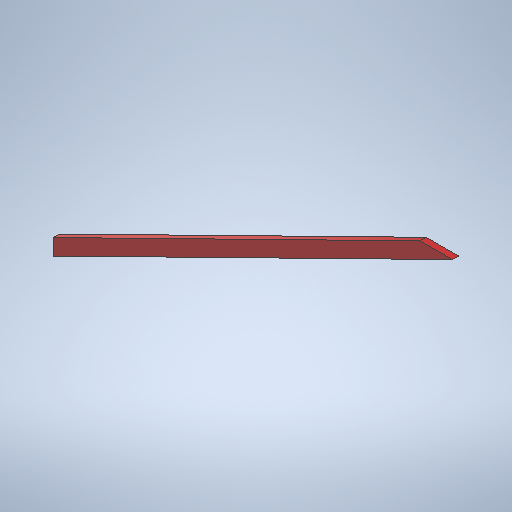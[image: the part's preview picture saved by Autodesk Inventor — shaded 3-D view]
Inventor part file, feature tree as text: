
AUTODESK INVENTOR PART (.ipt)
format: ipt  version: 2025.1 (Build 291241020, 241B)  size: 251,392 bytes
history: native  units: in
note: dims shown in document units (in); Inventor stores cm internally (conversion verified against a paired STEP export)
features: other x6, reference x3, extrude x1, sketch x1
ambient origin geometry x8: Origin, YZ Plane, XZ Plane, XY Plane, X Axis, Y Axis, Z Axis, Center Point
bodies: Solid1 (feature_tree)
feature tree (11):
  extrude  "Extrusion1"  Depth=1.5in TaperAngle=0.0deg
  sketch  "Sketch1"  dims[d0=3.5in d1=1.5in d2=0.0in]
  reference  "Reference1"
  reference  "Reference2"
  reference  "Reference3"
  other  "<userpath>\Documents\Tburn24\layer1\layer1.iam"
  other  "layer1.iam"
  other  "16'x2x4:2"
  other  "10'x2x4:6"
  other  "12'x2x4:1"
  other  "Finish1"
